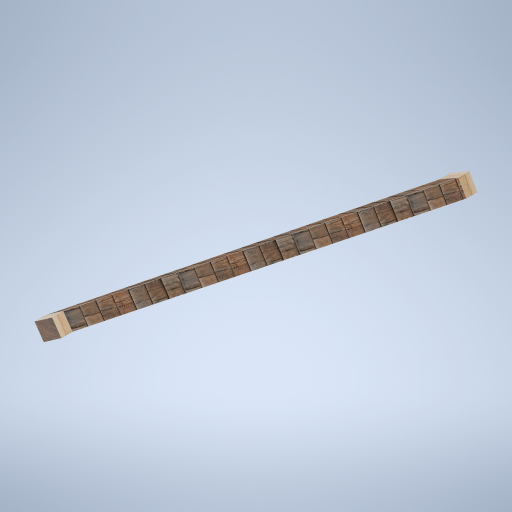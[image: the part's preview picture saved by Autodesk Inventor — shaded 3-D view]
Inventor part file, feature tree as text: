
AUTODESK INVENTOR PART (.ipt)
format: ipt  version: 2024.2 (Build 282272000, 272)  size: 319,488 bytes
history: native  units: mm
features: sketch x4, plane x2, extrude x2, loft x1, projected_geometry x1
ambient origin geometry x8: Origin, YZ Plane, XZ Plane, XY Plane, X Axis, Y Axis, Z Axis, Center Point
bodies: Solid1 (feature_tree)
feature tree (10):
  sketch  "Sketch5"  dims[d10=0.0mm d11=3749.0mm d12=0.0mm d13=90.0deg]
  plane  "Work Plane6"
  loft  "Loft1"
  extrude  "Extrusion1"  Depth=100.0mm TaperAngle=0.0deg
  extrude  "Extrusion2"  [1 undecoded]
  plane  "Work Plane5"
  sketch  "Sketch6"  dims[d14=0.0mm d15=90.0deg d16=100.0mm d17=0.0mm]
  sketch  "Sketch7"  dims[d18=100.0mm d19=0.0mm]
  sketch  "Sketch8"
  projected_geometry  "Projected Loop1"
note: 1 required parameter value undecoded (feature->parameter linkage not recoverable at this tier; creation-order binding heuristic only, values carry confidence <= 0.55)
